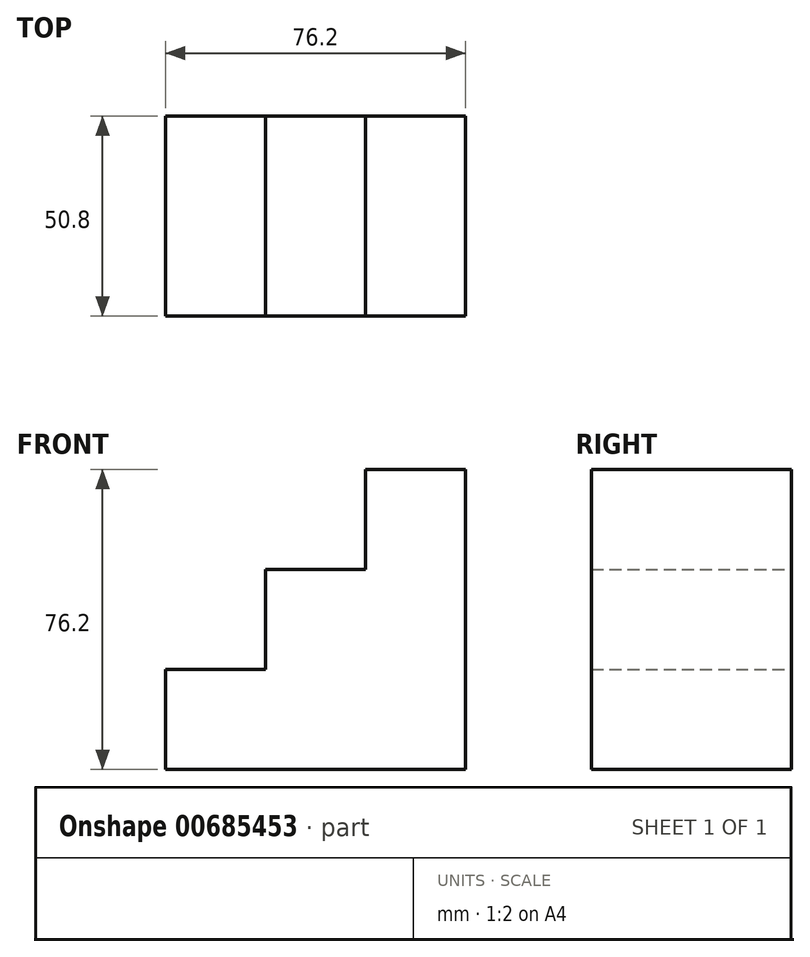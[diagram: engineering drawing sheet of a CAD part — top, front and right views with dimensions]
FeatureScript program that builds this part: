
annotation { "Feature Type Name" : "Feature", "Feature Type Description" : "" }
export const myFeature = defineFeature(function(context is Context, id is Id, definition is map)
    precondition{}
    {
        {
            var Q0;
            Q0=qCreatedBy(makeId("Front.planeOp"),FACE);
            var sketch = newSketch(context, id + "F0", { "sketchPlane" : qUnion([Q0])});
            skLineSegment(sketch, "E0", {"start": v(0, 0) * mm, "end": v(-76.2, 0) * mm});
            skLineSegment(sketch, "E1", {"start": v(0, 0) * mm, "end": v(0, 76.2) * mm});
            skLineSegment(sketch, "E2", {"start": v(-76.2, 0) * mm, "end": v(-76.2, 25.4) * mm});
            skLineSegment(sketch, "E3", {"start": v(0, 76.2) * mm, "end": v(-25.4, 76.2) * mm});
            skLineSegment(sketch, "E4", {"start": v(-25.4, 76.2) * mm, "end": v(-25.4, 50.8) * mm});
            skLineSegment(sketch, "E5", {"start": v(-25.4, 50.8) * mm, "end": v(-50.8, 50.8) * mm});
            skLineSegment(sketch, "E6", {"start": v(-50.8, 50.8) * mm, "end": v(-50.8, 25.4) * mm});
            skLineSegment(sketch, "E7", {"start": v(-50.8, 25.4) * mm, "end": v(-76.2, 25.4) * mm});
            skSolve(sketch);
        }
        {
            var Q0;
            Q0 = qSketchRegion(id + "F0", true);
            extrude(context, id + "F1", {"entities" : qUnion([Q0]), "depth" : 50.8 * mm, "offsetDistance" : 25.4 * mm});
        }
    });
